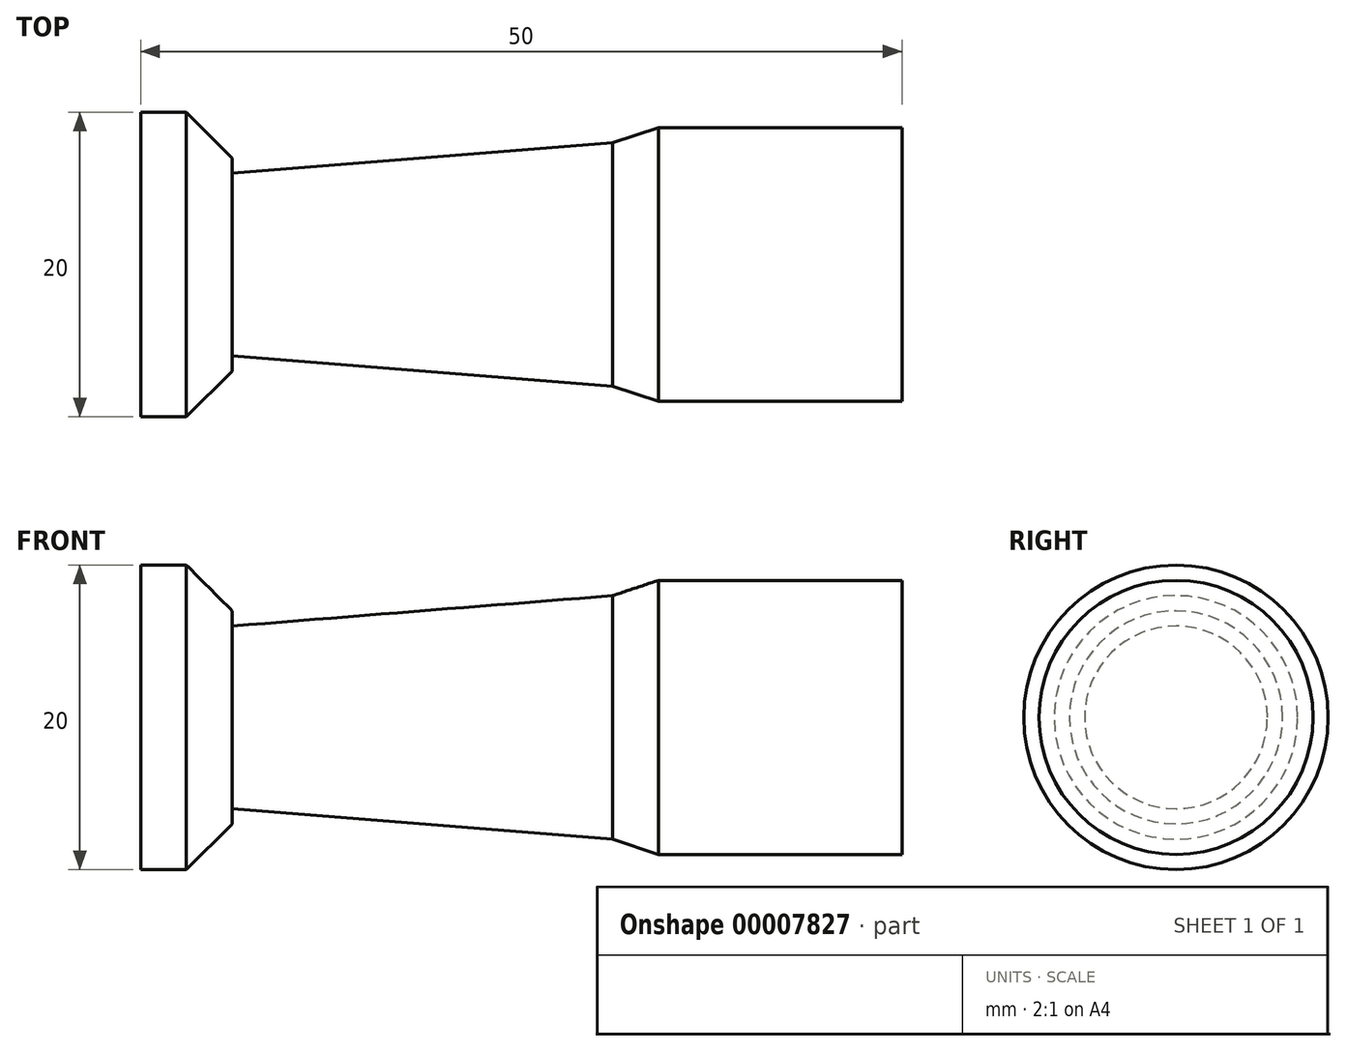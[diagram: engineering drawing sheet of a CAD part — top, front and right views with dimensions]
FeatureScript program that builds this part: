
annotation { "Feature Type Name" : "Feature", "Feature Type Description" : "" }
export const myFeature = defineFeature(function(context is Context, id is Id, definition is map)
    precondition{}
    {
        {
            var Q0;
            Q0=qCreatedBy(makeId("Front.planeOp"),FACE);
            var sketch = newSketch(context, id + "F0", { "sketchPlane" : qUnion([Q0])});
            skLineSegment(sketch, "E0", {"start": v(-11.86, 0) * mm, "end": v(38.14, 0) * mm});
            skLineSegment(sketch, "E1", {"start": v(38.14, 0) * mm, "end": v(38.14, -9) * mm});
            skLineSegment(sketch, "E2", {"start": v(38.14, -9) * mm, "end": v(22.14, -9) * mm});
            skLineSegment(sketch, "E3", {"start": v(22.14, -9) * mm, "end": v(19.14, -8) * mm});
            skLineSegment(sketch, "E4", {"start": v(19.14, -8) * mm, "end": v(-5.86, -6) * mm});
            skLineSegment(sketch, "E5", {"start": v(-5.86, -6) * mm, "end": v(-5.86, -10) * mm});
            skLineSegment(sketch, "E6", {"start": v(-5.86, -10) * mm, "end": v(-11.86, -10) * mm});
            skLineSegment(sketch, "E7", {"start": v(-11.86, -10) * mm, "end": v(-11.86, 0) * mm});
            skSolve(sketch);
        }
        {
            var Q0;
            Q0=makeQuery(id+"F0.imprint","IMPRINT",FACE,{"disambiguationData":[TD([[makeQuery(id+"F0.imprint","IMPRINT",EDGE,{"derivedFrom":sQuery(id+"F0.wireOp",EDGE,"E0")}),-1.0]])]});
            var Q1;
            Q1=sQuery(id+"F0.wireOp",EDGE,"E0");
            revolve(context, id + "F1", {"entities" : qUnion([Q0]), "axis" : qUnion([Q1]), "revolveType" : RevolveType.FULL});
        }
        {
            var Q0;
            Q0=makeQuery(id+"F1.opRevolve","SWEPT_EDGE",EDGE,{"disambiguationData":[OSD([sQuery(id+"F0.wireOp",EDGE,"E5"),sQuery(id+"F0.wireOp",EDGE,"E6")])]});
            chamfer(context, id + "F2", {"entities" : qUnion([Q0]), "width" : 3 * mm});
        }
    });
